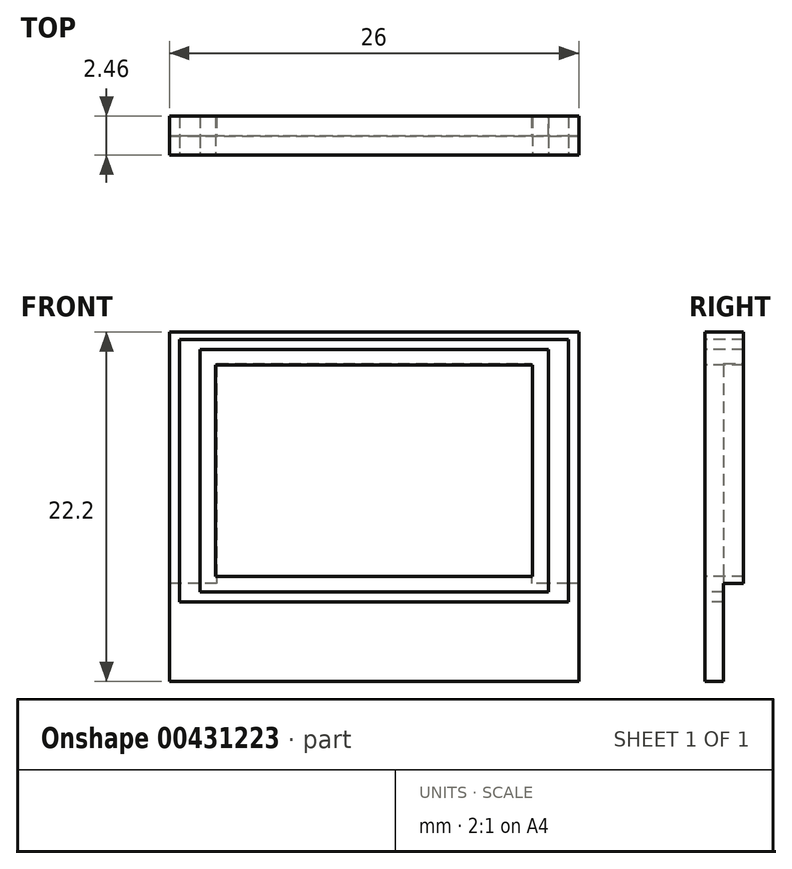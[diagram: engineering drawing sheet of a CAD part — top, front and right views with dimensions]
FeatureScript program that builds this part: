
annotation { "Feature Type Name" : "Feature", "Feature Type Description" : "" }
export const myFeature = defineFeature(function(context is Context, id is Id, definition is map)
    precondition{}
    {
        {
            var Q0;
            Q0=qCreatedBy(makeId("Front.planeOp"),FACE);
            var sketch = newSketch(context, id + "F0", { "sketchPlane" : qUnion([Q0])});
            skLineSegment(sketch, "E0.bottom", {"start": v(-10.07, 6.7) * mm, "end": v(10.07, 6.7) * mm});
            skLineSegment(sketch, "E0.top", {"start": v(-10.07, -6.7) * mm, "end": v(10.07, -6.71) * mm});
            skLineSegment(sketch, "E0.left", {"start": v(-10.07, 6.7) * mm, "end": v(-10.07, -6.71) * mm});
            skLineSegment(sketch, "E0.right", {"start": v(10.07, 6.7) * mm, "end": v(10.07, -6.7) * mm});
            skSolve(sketch);
        }
        {
            var Q0;
            Q0=qSketchRegion(id+"F0",true);
            extrude(context, id + "F1", {"entities" : qUnion([Q0]), "depth" : 2.46 * mm});
        }
        {
            var Q0;
            Q0=makeQuery(id+"F1.opExtrude","CAP_FACE",FACE,{"disambiguationData":[OSD([sQuery(id+"F0.wireOp",EDGE,"E0.bottom"),sQuery(id+"F0.wireOp",EDGE,"E0.top"),sQuery(id+"F0.wireOp",EDGE,"E0.left"),sQuery(id+"F0.wireOp",EDGE,"E0.right")])],"isStart":false});
            var sketch = newSketch(context, id + "F2", { "sketchPlane" : qUnion([Q0])});
            skLineSegment(sketch, "E1.0.0", {"start": v(-10.07, 6.7) * mm, "end": v(-10.07, -6.71) * mm});
            skLineSegment(sketch, "E1.0.1", {"start": v(-10.07, -6.7) * mm, "end": v(10.07, -6.71) * mm});
            skLineSegment(sketch, "E1.0.2", {"start": v(10.07, -6.7) * mm, "end": v(10.07, 6.7) * mm});
            skLineSegment(sketch, "E1.0.3", {"start": v(10.07, 6.7) * mm, "end": v(-10.07, 6.7) * mm});
            skLineSegment(sketch, "E2.bottom", {"start": v(-11.07, 7.71) * mm, "end": v(11.07, 7.7) * mm});
            skLineSegment(sketch, "E2.top", {"start": v(-11.07, -7.7) * mm, "end": v(11.07, -7.71) * mm});
            skLineSegment(sketch, "E2.left", {"start": v(-11.07, 7.7) * mm, "end": v(-11.07, -7.7) * mm});
            skLineSegment(sketch, "E2.right", {"start": v(11.07, 7.7) * mm, "end": v(11.07, -7.7) * mm});
            skSolve(sketch);
        }
        {
            var Q0;
            Q0=qSketchRegion(id+"F2",true);
            extrude(context, id + "F3", {"entities" : qUnion([Q0]), "oppositeDirection" : true, "depth" : 2.46 * mm});
        }
        {
            var Q0;
            Q0=makeQuery(id+"F1.opExtrude","CAP_FACE",FACE,{"disambiguationData":[OSD([sQuery(id+"F0.wireOp",EDGE,"E0.bottom"),sQuery(id+"F0.wireOp",EDGE,"E0.top"),sQuery(id+"F0.wireOp",EDGE,"E0.left"),sQuery(id+"F0.wireOp",EDGE,"E0.right")])],"isStart":false});
            var sketch = newSketch(context, id + "F4", { "sketchPlane" : qUnion([Q0])});
            skLineSegment(sketch, "E3.0.0", {"start": v(-11.07, 7.71) * mm, "end": v(-11.07, -7.7) * mm});
            skLineSegment(sketch, "E3.0.1", {"start": v(-11.07, -7.7) * mm, "end": v(11.07, -7.71) * mm});
            skLineSegment(sketch, "E3.0.2", {"start": v(11.07, -7.7) * mm, "end": v(11.07, 7.7) * mm});
            skLineSegment(sketch, "E3.0.3", {"start": v(11.07, 7.7) * mm, "end": v(-11.07, 7.71) * mm});
            skLineSegment(sketch, "E4.bottom", {"start": v(-12.35, 8.32) * mm, "end": v(12.35, 8.32) * mm});
            skLineSegment(sketch, "E4.top", {"start": v(-12.35, -8.32) * mm, "end": v(12.35, -8.32) * mm});
            skLineSegment(sketch, "E4.left", {"start": v(-12.35, 8.32) * mm, "end": v(-12.35, -8.32) * mm});
            skLineSegment(sketch, "E4.right", {"start": v(12.35, 8.32) * mm, "end": v(12.35, -8.32) * mm});
            skSolve(sketch);
        }
        {
            var Q0;
            Q0=qSketchRegion(id+"F4",true);
            extrude(context, id + "F5", {"entities" : qUnion([Q0]), "oppositeDirection" : true, "depth" : 2.46 * mm});
        }
        {
            var Q0;
            Q0=makeQuery(id+"F1.opExtrude","CAP_FACE",FACE,{"disambiguationData":[OSD([sQuery(id+"F0.wireOp",EDGE,"E0.bottom"),sQuery(id+"F0.wireOp",EDGE,"E0.top"),sQuery(id+"F0.wireOp",EDGE,"E0.left"),sQuery(id+"F0.wireOp",EDGE,"E0.right")])],"isStart":false});
            var sketch = newSketch(context, id + "F6", { "sketchPlane" : qUnion([Q0])});
            skLineSegment(sketch, "E5.bottom", {"start": v(-13, 8.82) * mm, "end": v(13, 8.83) * mm});
            skLineSegment(sketch, "E5.top", {"start": v(-13, -13.38) * mm, "end": v(13, -13.38) * mm});
            skLineSegment(sketch, "E5.left", {"start": v(-13, 8.83) * mm, "end": v(-13, -13.38) * mm});
            skLineSegment(sketch, "E5.right", {"start": v(13, 8.83) * mm, "end": v(13, -13.38) * mm});
            skLineSegment(sketch, "E6.0.0", {"start": v(-12.35, 8.32) * mm, "end": v(-12.35, -8.32) * mm});
            skLineSegment(sketch, "E6.0.1", {"start": v(-12.35, -8.32) * mm, "end": v(12.35, -8.32) * mm});
            skLineSegment(sketch, "E6.0.2", {"start": v(12.35, -8.32) * mm, "end": v(12.35, 8.32) * mm});
            skLineSegment(sketch, "E6.0.3", {"start": v(12.35, 8.32) * mm, "end": v(-12.35, 8.32) * mm});
            skSolve(sketch);
        }
        {
            var Q0;
            Q0=qSketchRegion(id+"F6",true);
            extrude(context, id + "F7", {"entities" : qUnion([Q0]), "oppositeDirection" : true, "depth" : 2.46 * mm});
        }
        {
            var Q0;
            Q0=qCreatedBy(makeId("Front.planeOp"),FACE);
            var sketch = newSketch(context, id + "F8", { "sketchPlane" : qUnion([Q0])});
            skLineSegment(sketch, "E7.bottom", {"start": v(-10, 6.82) * mm, "end": v(10, 6.83) * mm});
            skLineSegment(sketch, "E7.left", {"start": v(-10, 6.82) * mm, "end": v(-10, -7.15) * mm});
            skLineSegment(sketch, "E7.right", {"start": v(10, 6.82) * mm, "end": v(10, -7.15) * mm});
            skLineSegment(sketch, "E8", {"start": v(13, -7.15) * mm, "end": v(10, -7.15) * mm});
            skLineSegment(sketch, "E9.0", {"start": v(-13, -7.15) * mm, "end": v(-13, -13.38) * mm});
            skLineSegment(sketch, "E10.0", {"start": v(13, -7.15) * mm, "end": v(13, -13.38) * mm});
            skPoint(sketch, "E11.orphan", {"position": v(-13, 8.83) * mm});
            skLineSegment(sketch, "E12.trimOffspring", {"start": v(-10, -7.15) * mm, "end": v(-13, -7.15) * mm});
            skPoint(sketch, "E13.orphan", {"position": v(13, 8.83) * mm});
            skLineSegment(sketch, "E14", {"start": v(-13, -13.38) * mm, "end": v(13, -13.38) * mm});
            skSolve(sketch);
        }
        {
            var Q0;
            Q0=qSketchRegion(id+"F8",true);
            extrude(context, id + "F9", {"entities" : qUnion([Q0]), "operationType" : NewBodyOperationType.REMOVE, "depth" : 1.27 * mm});
        }
    });
